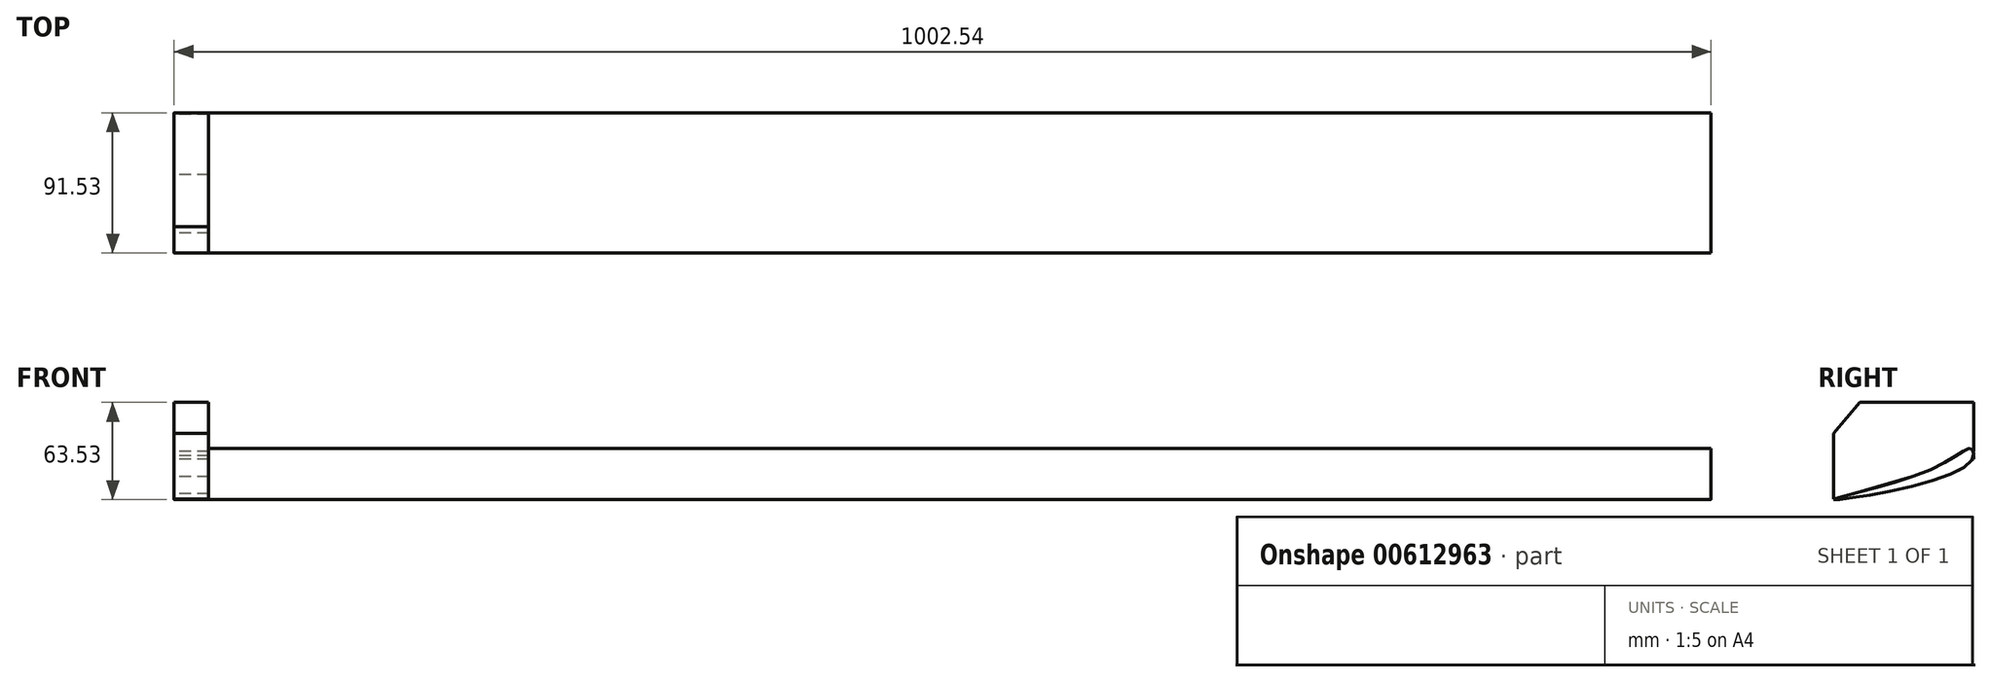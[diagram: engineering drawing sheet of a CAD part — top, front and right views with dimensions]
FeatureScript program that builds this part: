
annotation { "Feature Type Name" : "Feature", "Feature Type Description" : "" }
export const myFeature = defineFeature(function(context is Context, id is Id, definition is map)
    precondition{}
    {
        {
            var Q0;
            Q0=qCreatedBy(makeId("Right.planeOp"),FACE);
            var sketch = newSketch(context, id + "F0", { "sketchPlane" : qUnion([Q0])});
            skSolve(sketch);
        }
        {
            var Q0;
            Q0=qCreatedBy(makeId("Right.planeOp"),FACE);
            var sketch = newSketch(context, id + "F1", { "sketchPlane" : qUnion([Q0])});
            skFitSpline(sketch, "E0", {"points": [v(-52.5, 11.94) * mm, v(34.04, 33.98) * mm, v(37.51, 45) * mm, v(12.61, 32.35) * mm, v(-52.5, 11.94) * mm]});
            skSolve(sketch);
        }
        {
            var Q0;
            Q0=qCreatedBy(makeId("Right.planeOp"),FACE);
            var sketch = newSketch(context, id + "F2", { "sketchPlane" : qUnion([Q0])});
            skLineSegment(sketch, "E1", {"start": v(-52.56, 12.14) * mm, "end": v(-52.56, 55.21) * mm});
            skLineSegment(sketch, "E2", {"start": v(-52.56, 55.21) * mm, "end": v(-35.62, 75.42) * mm});
            skLineSegment(sketch, "E3", {"start": v(-35.62, 75.42) * mm, "end": v(38.68, 75.42) * mm});
            skLineSegment(sketch, "E4", {"start": v(38.68, 75.42) * mm, "end": v(38.68, 38.47) * mm});
            skLineSegment(sketch, "E5", {"start": v(-52.56, 12.14) * mm, "end": v(38.68, 38.47) * mm});
            skSolve(sketch);
        }
        {
            var Q0;
            Q0 = qSketchRegion(id + "F2", true);
            extrude(context, id + "F3", {"entities" : qUnion([Q0]), "depth" : 20 * mm, "offsetDistance" : 25.4 * mm});
        }
        {
            var Q0;
            Q0 = qSketchRegion(id + "F1", true);
            extrude(context, id + "F4", {"entities" : qUnion([Q0]), "operationType" : NewBodyOperationType.ADD, "depth" : 1000 * mm, "offsetDistance" : 25.4 * mm});
        }
        {
            var Q0;
            Q0 = qSketchRegion(id + "F0", true);
            var Q1;
            Q1=makeQuery(id+"F4.boolean.opBoolean","MERGE",FACE,{"derivedFrom":[makeQuery(id+"F3.opExtrude","CAP_FACE",FACE,{"disambiguationData":[OSD([sQuery(id+"F2.wireOp",EDGE,"E1"),sQuery(id+"F2.wireOp",EDGE,"E2"),sQuery(id+"F2.wireOp",EDGE,"E3"),sQuery(id+"F2.wireOp",EDGE,"E4"),sQuery(id+"F2.wireOp",EDGE,"E5")])],"isStart":true}),makeQuery(id+"F4.opExtrude","CAP_FACE",FACE,{"disambiguationData":[OSD([sQuery(id+"F1.wireOp",EDGE,"E0")])],"isStart":true})]});
            extrude(context, id + "F5", {"entities" : qUnion([Q0, Q1]), "operationType" : NewBodyOperationType.ADD, "depth" : 2.54 * mm, "offsetDistance" : 25.4 * mm});
        }
    });
